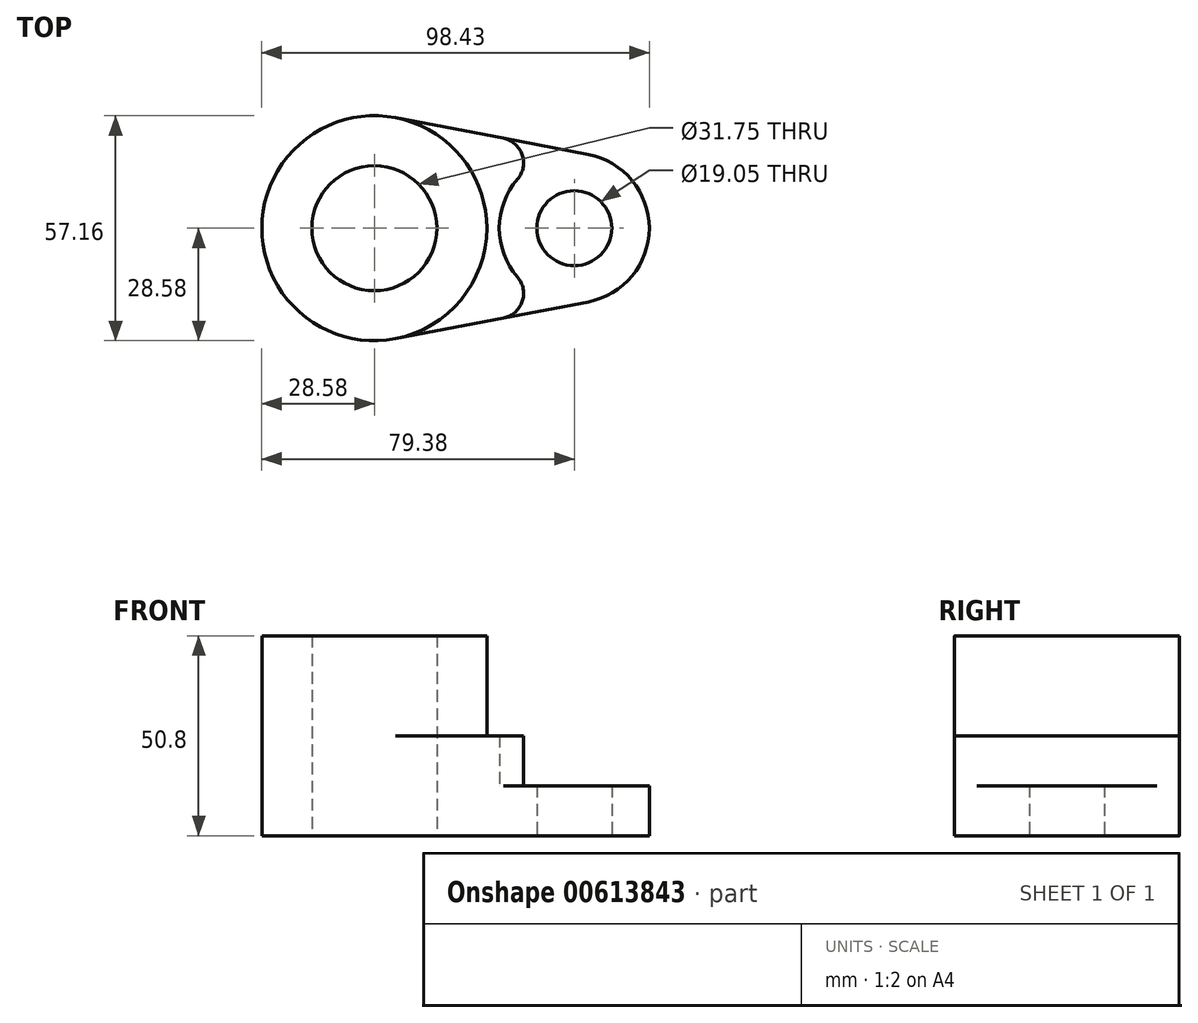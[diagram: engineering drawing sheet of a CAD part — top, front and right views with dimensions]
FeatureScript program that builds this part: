
annotation { "Feature Type Name" : "Feature", "Feature Type Description" : "" }
export const myFeature = defineFeature(function(context is Context, id is Id, definition is map)
    precondition{}
    {
        {
            var Q0;
            Q0=qCreatedBy(makeId("Top.planeOp"),FACE);
            var sketch = newSketch(context, id + "F0", { "sketchPlane" : qUnion([Q0])});
            skCircle(sketch, "E0", {"center": v(0, 0) * mm, "radius": 28.58 * mm});
            skCircle(sketch, "E1", {"center": v(0, 0) * mm, "radius": 15.88 * mm});
            skCircle(sketch, "E2", {"center": v(50.8, 0) * mm, "radius": 19.05 * mm});
            skCircle(sketch, "E3", {"center": v(50.8, 0) * mm, "radius": 9.53 * mm});
            skLineSegment(sketch, "E4", {"start": v(5.36, 28.07) * mm, "end": v(54.37, 18.71) * mm});
            skLineSegment(sketch, "E5", {"start": v(5.36, -28.07) * mm, "end": v(54.37, -18.71) * mm});
            skSolve(sketch);
        }
        {
            var Q0;
            {var subQ0=sQuery(id+"F0.wireOp",EDGE,"E4");Q0=makeQuery(id+"F0.imprint","IMPRINT",FACE,{"disambiguationData":[TD([[makeQuery(id+"F0.imprint","IMPRINT",EDGE,{"derivedFrom":subQ0}),-1.0]])]});}
            var Q1;
            Q1=makeQuery(id+"F0.imprint","IMPRINT",FACE,{"disambiguationData":[TD([[makeQuery(id+"F0.imprint","IMPRINT",EDGE,{"derivedFrom":sQuery(id+"F0.wireOp",EDGE,"E1")}),-1.0]])]});
            extrude(context, id + "F1", {"entities" : qUnion([Q0, Q1]), "depth" : 25.4 * mm, "offsetDistance" : 25.4 * mm});
        }
        {
            var Q0;
            Q0=makeQuery(id+"F0.imprint","IMPRINT",FACE,{"disambiguationData":[TD([[makeQuery(id+"F0.imprint","IMPRINT",EDGE,{"derivedFrom":sQuery(id+"F0.wireOp",EDGE,"E1")}),-1.0]])]});
            extrude(context, id + "F2", {"entities" : qUnion([Q0]), "operationType" : NewBodyOperationType.ADD, "depth" : 50.8 * mm, "offsetDistance" : 25.4 * mm});
        }
        {
            var Q0;
            Q0=makeQuery(id+"F0.imprint","IMPRINT",FACE,{"disambiguationData":[TD([[makeQuery(id+"F0.imprint","IMPRINT",EDGE,{"derivedFrom":sQuery(id+"F0.wireOp",EDGE,"E3")}),-1.0]])]});
            extrude(context, id + "F3", {"entities" : qUnion([Q0]), "operationType" : NewBodyOperationType.ADD, "depth" : 12.7 * mm, "offsetDistance" : 25.4 * mm});
        }
        {
            var Q0;
            {var subQ0=sQuery(id+"F0.wireOp",EDGE,"E2");var subQ1=sQuery(id+"F0.wireOp",EDGE,"E5");Q0=makeQuery(id+"F3.boolean.opBoolean","SPLIT",EDGE,{"disambiguationData":[topologyDisambiguationEdgeConnected([makeQuery(id+"F1.opExtrude","SWEPT_FACE",FACE,{"disambiguationData":[OSD([subQ0])]})])],"derivedFrom":makeQuery(id+"F1.opExtrude","SWEPT_EDGE",EDGE,{"disambiguationData":[OSD([subQ0,subQ1])]})});}
            var Q1;
            {var subQ0=sQuery(id+"F0.wireOp",EDGE,"E2");var subQ1=sQuery(id+"F0.wireOp",EDGE,"E4");Q1=makeQuery(id+"F3.boolean.opBoolean","SPLIT",EDGE,{"disambiguationData":[topologyDisambiguationEdgeConnected([makeQuery(id+"F1.opExtrude","SWEPT_FACE",FACE,{"disambiguationData":[OSD([subQ0])]})])],"derivedFrom":makeQuery(id+"F1.opExtrude","SWEPT_EDGE",EDGE,{"disambiguationData":[OSD([subQ0,subQ1])]})});}
            fillet(context, id + "F4", {"entities" : qUnion([Q0, Q1]), "radius" : 6.35 * mm, "tangentPropagation" : true, "allowEdgeOverflow" : false});
        }
    });
